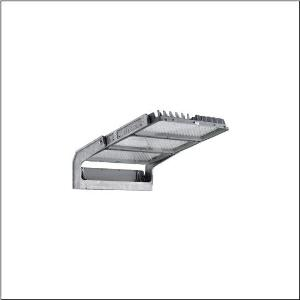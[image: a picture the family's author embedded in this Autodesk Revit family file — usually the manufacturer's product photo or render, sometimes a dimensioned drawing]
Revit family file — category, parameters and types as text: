
# Revit family: floodlight_fl_11_maxi_pro___rs08_5xa779124l01gb_5403
name_source: partatom
category: Lighting Fixtures
units: mm (PartAtom-declared; Revit-internal decimal feet)

## family parameters
Cut with Voids When Loaded = No
Host = Face
Light Source = No
Part Type = Normal
Room Calculation Point = No
Round Connector Dimension = Use Diameter
Shared = No

## types (1)
- --- (1 x LED, 121700 lm, 1227.1 W, 5700K)
    Apparent Load = 1227 VA
    CIE Flux Codes = 70 87 98 100 100
    Color Rendering = 90
    Color Temperature = 5700K
    Default Elevation = 1800 mm
    Description = Floodlight FL 11  maxi  pro floodlight; light control with lens of PMMA; cover panel of toughened safety glass, transparent; light distribution: RS08, rotationally symmetric direct distribution, LED; colour temperature: 5700K, rated luminous flux: 121.700lm, colour rendering: CRI > 90, light colour: 957; luminous efficacy: 99lm/W; brightness control: DALI 2; with terminal, 5-pole, max. 2.5mm², mains connection: 220..240V/380..400V AC, 50/60Hz, surge voltage resistance: line to ground: 10kV, LED service life up to 100,000h L90. Typical operating time: 1000h per year., ECG replaceable separately, LED unit replaceable without ESD environment, dustproof LED module, dimming range 10..100%; 1227W floodlight with 3x LED unit of diecast aluminium, coated grey; length: 1.003mm / width: 651mm / height: 338mm; mounting bracket, of diecast aluminium, uncoated, natural, equipment: Power, protection rating (complete): IP66; insulation class (complete): insulation class I (protective earthing); certification: CE, ENEC, VDE; ball protection: ball impact resistant, only for outdoor installations in the designated locations, permissible operating ambient temperature: -45..+55°C, permissible storage temperature: -40..+85°Cpackaging unit: 1 piece

Light Distribution: RS08
    Height = 320 mm
    Lamp = 1 x LED
    Lamp Light Flux = 121700 lm
    Lamp Power = 1227.1 W
    Lamp count = 1
    Length = 1002 mm
    Luminous efficacy = 99 lm/W
    Manufacturer = Siteco
    ModVariant = No
    Model = 5XA779124L01GB
    Mounting Place = Ceiling
    Mounting Type = Surface mounted
    Number of Poles = 1
    OnlyDefault = Yes
    Power Factor = 1
    Product Name = Floodlight FL 11 maxi pro | RS08
    Product group = floodlight | ceiling mounted
    ProductGroupID = 303
    Protection Class = Protection class I
    Protection Degree = IP 66
    RLX_Detail_Level = 1
    RLX_Emergency_Light_Flux = 0 lm
    RLX_Emergency_Type = 0
    RLX_Emergency_Type_DB = No
    RlxData = <blob elided: 40213 chars, md5=4f886592>
    Socket = socket
    Standby Power = 0 W
    System Light Flux = 121700 lm
    System Power = 1227 W
    Type Comments = factory setting: luminous flux: 100 % | dim-lin: 254 | 840 mA
    Type Image = l_1356210.jpg
    URL = http://relux.com
    VarID = @adj_040229
    Voltage = 0 V
    Weight = 0.00 kg
    Width = 655 mm

## geometry (parser evidence)
native form markers: Blend x4, Sweep x12
no freeform markers — native parametric forms only
